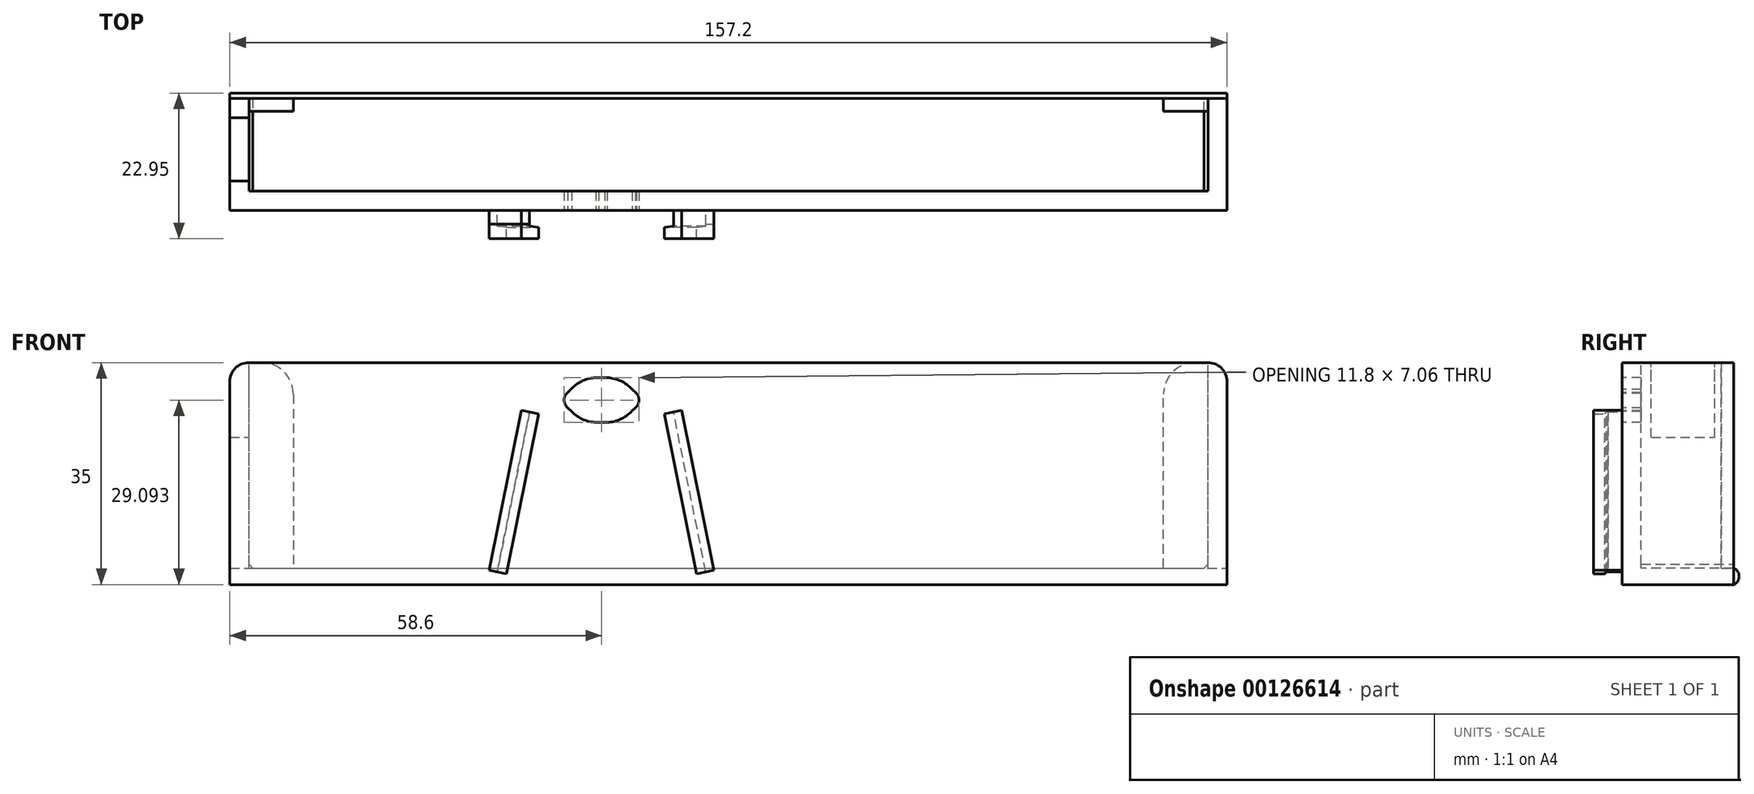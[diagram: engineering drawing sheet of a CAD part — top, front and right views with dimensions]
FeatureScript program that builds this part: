
annotation { "Feature Type Name" : "Feature", "Feature Type Description" : "" }
export const myFeature = defineFeature(function(context is Context, id is Id, definition is map)
    precondition{}
    {
        {
            var Q0;
            Q0=qCreatedBy(makeId("Front.planeOp"),FACE);
            var sketch = newSketch(context, id + "F0", { "sketchPlane" : qUnion([Q0])});
            skLineSegment(sketch, "E0", {"start": v(-29.32, 18.5) * mm, "end": v(-29.32, -6.7) * mm, "construction": true});
            skLineSegment(sketch, "E1", {"start": v(-29.32, -6.7) * mm, "end": v(-34.42, -6.7) * mm, "construction": true});
            skLineSegment(sketch, "E2", {"start": v(-29.32, 18.5) * mm, "end": v(-34.42, -6.7) * mm});
            skLineSegment(sketch, "E3", {"start": v(-34.42, -6.7) * mm, "end": v(-35.7, -6.44) * mm});
            skLineSegment(sketch, "E4", {"start": v(-35.7, -6.44) * mm, "end": v(-30.6, 18.76) * mm});
            skLineSegment(sketch, "E5", {"start": v(-29.32, 18.5) * mm, "end": v(-30.6, 18.76) * mm});
            skLineSegment(sketch, "E6", {"start": v(-30.6, 18.76) * mm, "end": v(-35.7, -6.44) * mm});
            skLineSegment(sketch, "E7", {"start": v(-29.32, 18.5) * mm, "end": v(-6.62, 18.5) * mm, "construction": true});
            skLineSegment(sketch, "E8", {"start": v(-6.62, 18.5) * mm, "end": v(-6.62, -6.7) * mm, "construction": true});
            skLineSegment(sketch, "E9", {"start": v(-6.62, -6.7) * mm, "end": v(-1.52, -6.7) * mm, "construction": true});
            skLineSegment(sketch, "E10", {"start": v(-1.52, -6.7) * mm, "end": v(-6.62, 18.5) * mm});
            skLineSegment(sketch, "E11", {"start": v(-6.62, 18.5) * mm, "end": v(-5.34, 18.76) * mm});
            skLineSegment(sketch, "E12", {"start": v(-5.34, 18.76) * mm, "end": v(-0.24, -6.44) * mm});
            skLineSegment(sketch, "E13", {"start": v(-1.52, -6.7) * mm, "end": v(-0.24, -6.44) * mm});
            skPoint(sketch, "E14.orphan", {"position": v(-0.2, -6.7) * mm});
            skLineSegment(sketch, "E15", {"start": v(-6.62, 18.5) * mm, "end": v(-6.62, 20.4) * mm, "construction": true});
            skLineSegment(sketch, "E16", {"start": v(-6.62, 20.4) * mm, "end": v(-29.32, 20.4) * mm, "construction": true});
            skLineSegment(sketch, "E17", {"start": v(-29.32, 20.4) * mm, "end": v(-29.32, 18.5) * mm, "construction": true});
            skLineSegment(sketch, "E18", {"start": v(-17.97, 20.4) * mm, "end": v(-17.97, 23.9) * mm, "construction": true});
            skLineSegment(sketch, "E19", {"start": v(-17.97, 23.9) * mm, "end": v(-17.97, 20.4) * mm, "construction": true});
            skLineSegment(sketch, "E20", {"start": v(-17.97, 20.4) * mm, "end": v(-17.97, 16.9) * mm, "construction": true});
            skPoint(sketch, "E20.endSnap0", {"position": v(-17.97, 18.5) * mm});
            skLineSegment(sketch, "E21", {"start": v(-17.97, 20.4) * mm, "end": v(-12.07, 20.4) * mm, "construction": true});
            skLineSegment(sketch, "E22", {"start": v(-17.97, 20.4) * mm, "end": v(-23.87, 20.4) * mm, "construction": true});
            skArc(sketch, "E23", {"start": v(-12.89, 19.03) * mm, "mid": v(-12.88, 19.03) * mm, "end": v(-12.87, 19.04) * mm});
            skLineSegment(sketch, "E24", {"start": v(-12.07, 20.4) * mm, "end": v(-13.64, 20.4) * mm, "construction": true});
            skLineSegment(sketch, "E25", {"start": v(-23.87, 20.4) * mm, "end": v(-22.3, 20.4) * mm, "construction": true});
            skArc(sketch, "E26", {"start": v(-23.32, 21.6) * mm, "mid": v(-23.87, 20.4) * mm, "end": v(-23.3, 19.2) * mm});
            skLineSegment(sketch, "E27", {"start": v(-23.34, 21.58) * mm, "end": v(-23.33, 21.58) * mm});
            skLineSegment(sketch, "E28", {"start": v(-23.37, 19.26) * mm, "end": v(-23.35, 19.24) * mm});
            skLineSegment(sketch, "E29", {"start": v(-17.97, 16.9) * mm, "end": v(-17.97, -14.32) * mm, "construction": true});
            skLineSegment(sketch, "E30", {"start": v(-6.62, -6.7) * mm, "end": v(-17.97, -6.7) * mm, "construction": true});
            skLineSegment(sketch, "E31", {"start": v(-17.97, -6.7) * mm, "end": v(-17.97, -8.7) * mm, "construction": true});
            skLineSegment(sketch, "E32", {"start": v(-17.97, -8.7) * mm, "end": v(80.63, -8.7) * mm});
            skLineSegment(sketch, "E33", {"start": v(80.63, -8.7) * mm, "end": v(-76.57, -8.7) * mm});
            skLineSegment(sketch, "E34.bottom", {"start": v(-76.57, -8.7) * mm, "end": v(80.63, -8.7) * mm});
            skLineSegment(sketch, "E34.top", {"start": v(-76.57, 26.3) * mm, "end": v(80.63, 26.3) * mm});
            skLineSegment(sketch, "E34.left", {"start": v(-76.57, -8.7) * mm, "end": v(-76.57, 26.3) * mm});
            skLineSegment(sketch, "E34.right", {"start": v(80.63, -8.7) * mm, "end": v(80.63, 26.3) * mm});
            skArc(sketch, "E35", {"start": v(-13.16, 22.11) * mm, "mid": v(-14.93, 23.4) * mm, "end": v(-17.06, 23.93) * mm});
            skArc(sketch, "E36", {"start": v(-18.87, 23.93) * mm, "mid": v(-20.87, 23.47) * mm, "end": v(-22.56, 22.33) * mm});
            skArc(sketch, "E37", {"start": v(-17.47, 16.87) * mm, "mid": v(-15.11, 17.33) * mm, "end": v(-13.15, 18.7) * mm});
            skLineSegment(sketch, "E38", {"start": v(-12.48, 21.46) * mm, "end": v(-13.16, 22.11) * mm});
            skLineSegment(sketch, "E39", {"start": v(-12.48, 19.35) * mm, "end": v(-13.69, 18.2) * mm});
            skLineSegment(sketch, "E40", {"start": v(-23.46, 19.35) * mm, "end": v(-22.4, 18.32) * mm});
            skLineSegment(sketch, "E41", {"start": v(-23.46, 21.46) * mm, "end": v(-22.56, 22.33) * mm});
            skLineSegment(sketch, "E42", {"start": v(-17.06, 23.93) * mm, "end": v(-18.87, 23.93) * mm});
            skLineSegment(sketch, "E43", {"start": v(-17.47, 16.87) * mm, "end": v(-18.77, 16.87) * mm});
            skArc(sketch, "E44.trimOffspring", {"start": v(-12.64, 19.2) * mm, "mid": v(-12.07, 20.3) * mm, "end": v(-12.48, 21.46) * mm});
            skArc(sketch, "E45.trimOffspring", {"start": v(-22.7, 18.62) * mm, "mid": v(-20.75, 17.3) * mm, "end": v(-18.43, 16.87) * mm});
            skSolve(sketch);
        }
        {
            var Q0;
            Q0=makeQuery(id+"F0.imprint","IMPRINT",FACE,{"disambiguationData":[TD([[makeQuery(id+"F0.imprint","IMPRINT",EDGE,{"derivedFrom":sQuery(id+"F0.wireOp",EDGE,"E10")}),-1.0]])]});
            var Q1;
            Q1=makeQuery(id+"F0.imprint","IMPRINT",FACE,{"disambiguationData":[TD([[makeQuery(id+"F0.imprint","IMPRINT",EDGE,{"derivedFrom":sQuery(id+"F0.wireOp",EDGE,"E2")}),-1.0]])]});
            extrude(context, id + "F1", {"entities" : qUnion([Q0, Q1]), "depth" : 2.2 * mm});
        }
        {
            var Q0;
            Q0=makeQuery(id+"F1.opExtrude","SWEPT_FACE",FACE,{"disambiguationData":[OSD([sQuery(id+"F0.wireOp",EDGE,"E5")])]});
            var sketch = newSketch(context, id + "F2", { "sketchPlane" : qUnion([Q0])});
            skLineSegment(sketch, "E46", {"start": v(-33.7, 0) * mm, "end": v(-33.7, -4.5) * mm});
            skLineSegment(sketch, "E47", {"start": v(-33.7, -4.5) * mm, "end": v(-30.9, -4.5) * mm});
            skLineSegment(sketch, "E48", {"start": v(-30.9, -4.5) * mm, "end": v(-30.9, -2.7) * mm});
            skLineSegment(sketch, "E49", {"start": v(-32.4, 0) * mm, "end": v(-32.4, -2.5) * mm, "construction": true});
            skLineSegment(sketch, "E50", {"start": v(-30.9, -2.7) * mm, "end": v(-32.4, -2.5) * mm});
            skLineSegment(sketch, "E51", {"start": v(-32.4, -2.5) * mm, "end": v(-32.4, 0) * mm});
            skLineSegment(sketch, "E52", {"start": v(-32.4, -2.2) * mm, "end": v(-33.7, -2.2) * mm});
            skSolve(sketch);
        }
        {
            var Q0;
            Q0 = qSketchRegion(id + "F2", true);
            var Q1;
            {var subQ0=sQuery(id+"F2.wireOp",EDGE,"E47");Q1=makeQuery(id+"F2.imprint","IMPRINT",FACE,{"disambiguationData":[TD([[makeQuery(id+"F2.imprint","IMPRINT",EDGE,{"derivedFrom":subQ0}),1.0]])]});}
            extrude(context, id + "F3", {"entities" : qUnion([Q0, Q1]), "oppositeDirection" : true, "depth" : 25.7 * mm});
        }
        {
            var Q0;
            Q0=makeQuery(id+"F1.opExtrude","SWEPT_FACE",FACE,{"disambiguationData":[OSD([sQuery(id+"F0.wireOp",EDGE,"E11")])]});
            var sketch = newSketch(context, id + "F4", { "sketchPlane" : qUnion([Q0])});
            skLineSegment(sketch, "E53", {"start": v(-1.52, 0) * mm, "end": v(-1.52, -4.5) * mm});
            skLineSegment(sketch, "E54", {"start": v(-1.52, -4.5) * mm, "end": v(-4.32, -4.5) * mm});
            skLineSegment(sketch, "E55", {"start": v(-4.32, -4.5) * mm, "end": v(-4.32, -2.7) * mm});
            skLineSegment(sketch, "E56", {"start": v(-2.82, 0) * mm, "end": v(-2.82, -2.5) * mm, "construction": true});
            skLineSegment(sketch, "E57", {"start": v(-4.32, -2.7) * mm, "end": v(-2.82, -2.5) * mm});
            skLineSegment(sketch, "E58", {"start": v(-2.82, -2.5) * mm, "end": v(-2.82, -2.2) * mm});
            skSolve(sketch);
        }
        {
            var Q0;
            Q0 = qSketchRegion(id + "F4", true);
            var Q1;
            {var subQ1=sQuery(id+"F4.wireOp",EDGE,"E54");Q1=makeQuery(id+"F4.imprint","IMPRINT",FACE,{"disambiguationData":[TD([[makeQuery(id+"F4.imprint","IMPRINT",EDGE,{"derivedFrom":subQ1}),-1.0]])]});}
            extrude(context, id + "F5", {"entities" : qUnion([Q0, Q1]), "operationType" : NewBodyOperationType.ADD, "oppositeDirection" : true, "depth" : 25.7 * mm});
        }
        {
            var Q0;
            Q0 = qSketchRegion(id + "F0", true);
            var Q1;
            Q1=makeQuery(id+"F0.imprint","IMPRINT",FACE,{"disambiguationData":[TD([[makeQuery(id+"F0.imprint","IMPRINT",EDGE,{"derivedFrom":sQuery(id+"F0.wireOp",EDGE,"E2")}),-1.0]])]});
            var Q2;
            Q2=makeQuery(id+"F0.imprint","IMPRINT",FACE,{"disambiguationData":[TD([[makeQuery(id+"F0.imprint","IMPRINT",EDGE,{"derivedFrom":sQuery(id+"F0.wireOp",EDGE,"E10")}),-1.0]])]});
            extrude(context, id + "F6", {"entities" : qUnion([Q0, Q1, Q2]), "oppositeDirection" : true, "depth" : 3 * mm});
        }
        {
            var Q0;
            Q0=makeQuery(id+"F6.opExtrude","CAP_FACE",FACE,{"disambiguationData":[OSD([sQuery(id+"F0.wireOp",EDGE,"MNrqED6R-0Bs3-LNVi-oEKI-MaJAXrPDSpCK"),sQuery(id+"F0.wireOp",EDGE,"FX8ncu83-0Qzv-e0OL-q1TA-2oPik7mIZz2Z"),sQuery(id+"F0.wireOp",EDGE,"E23"),sQuery(id+"F0.wireOp",EDGE,"E26"),sQuery(id+"F0.wireOp",EDGE,"E27"),sQuery(id+"F0.wireOp",EDGE,"E28"),sQuery(id+"F0.wireOp",EDGE,"ljumUwIM-9yZB-9kN5-kGQy-0t9YJfCgj0Kk"),sQuery(id+"F0.wireOp",EDGE,"Kp9V1Czn-WVNw-DR18-KSKj-JMUbyk1VQTje"),sQuery(id+"F0.wireOp",EDGE,"E34.bottom"),sQuery(id+"F0.wireOp",EDGE,"E34.top"),sQuery(id+"F0.wireOp",EDGE,"E34.left"),sQuery(id+"F0.wireOp",EDGE,"E34.right")])],"isStart":false});
            var sketch = newSketch(context, id + "F7", { "sketchPlane" : qUnion([Q0])});
            skLineSegment(sketch, "E59.1", {"start": v(73.57, -6.1) * mm, "end": v(73.57, 40.7) * mm});
            skLineSegment(sketch, "E59.2", {"start": v(73.57, -6.1) * mm, "end": v(-77.63, -6.1) * mm});
            skLineSegment(sketch, "E59.3", {"start": v(-77.63, -6.1) * mm, "end": v(-77.63, 40.7) * mm});
            skLineSegment(sketch, "E60", {"start": v(73.57, 26.3) * mm, "end": v(73.57, 40.7) * mm});
            skLineSegment(sketch, "E61", {"start": v(-77.63, -6.1) * mm, "end": v(-77.63, 26.3) * mm});
            skSolve(sketch);
        }
        {
            var Q0;
            Q0 = qSketchRegion(id + "F7", true);
            var Q1;
            Q1=makeQuery(id+"F7.imprint","IMPRINT",FACE,{"disambiguationData":[TD([[makeQuery(id+"F7.imprint","IMPRINT",EDGE,{"derivedFrom":sQuery(id+"F7.wireOp",EDGE,"E59.1")}),-1.0]])]});
            extrude(context, id + "F8", {"entities" : qUnion([Q0, Q1]), "operationType" : NewBodyOperationType.ADD, "depth" : (12 + 2.6) * mm});
        }
        {
            var Q0;
            Q0=makeQuery(id+"F8.opExtrude","CAP_FACE",FACE,{"disambiguationData":[OSD([sQuery(id+"F0.wireOp",EDGE,"E34.bottom"),sQuery(id+"F0.wireOp",EDGE,"E34.top"),sQuery(id+"F0.wireOp",EDGE,"E34.left"),sQuery(id+"F0.wireOp",EDGE,"E34.right"),sQuery(id+"F7.wireOp",EDGE,"E59.1"),sQuery(id+"F7.wireOp",EDGE,"E59.2"),sQuery(id+"F7.wireOp",EDGE,"E59.3"),sQuery(id+"F7.wireOp",EDGE,"EL1yQ1mo-xAsi-Qadm-DahA-Dr1vwk5fQx9r"),sQuery(id+"F7.wireOp",EDGE,"E60")])],"isStart":false});
            var sketch = newSketch(context, id + "F9", { "sketchPlane" : qUnion([Q0])});
            skLineSegment(sketch, "E62", {"start": v(76.57, 26.3) * mm, "end": v(66.57, 26.3) * mm});
            skLineSegment(sketch, "E63", {"start": v(66.57, 26.3) * mm, "end": v(66.57, -6.1) * mm});
            skLineSegment(sketch, "E64", {"start": v(-77.63, 26.3) * mm, "end": v(-70.63, 26.3) * mm});
            skLineSegment(sketch, "E65", {"start": v(-70.63, -6.1) * mm, "end": v(-70.63, 26.3) * mm});
            skLineSegment(sketch, "E66", {"start": v(73.57, 26.3) * mm, "end": v(73.57, -6.1) * mm});
            skSolve(sketch);
        }
        {
            var Q0;
            Q0 = qSketchRegion(id + "F9", true);
            var Q1;
            {var subQ2=sQuery(id+"F9.wireOp",EDGE,"5CY6TRSu-ZqDC-SEN2-w5CQ-rCevLjkbbSBQ");Q1=makeQuery(id+"F9.imprint","IMPRINT",FACE,{"disambiguationData":[TD([[makeQuery(id+"F9.imprint","IMPRINT",EDGE,{"derivedFrom":subQ2}),-1.0]])]});}
            var Q2;
            Q2=makeQuery(id+"F9.imprint","IMPRINT",FACE,{"disambiguationData":[TD([[makeQuery(id+"F9.imprint","IMPRINT",EDGE,{"derivedFrom":sQuery(id+"F9.wireOp",EDGE,"E62")}),1.0]])]});
            var Q3;
            Q3=makeQuery(id+"F9.imprint","IMPRINT",FACE,{"disambiguationData":[TD([[makeQuery(id+"F9.imprint","IMPRINT",EDGE,{"derivedFrom":sQuery(id+"F9.wireOp",EDGE,"E64")}),-1.0]])]});
            extrude(context, id + "F10", {"entities" : qUnion([Q0, Q1, Q2, Q3]), "oppositeDirection" : true, "depth" : 2 * mm});
        }
        {
            var Q0;
            {var subQ0=sQuery(id+"F0.wireOp",EDGE,"E34.right");Q0=makeQuery(id+"F8.boolean.opBoolean","MERGE",FACE,{"derivedFrom":[makeQuery(id+"F6.opExtrude","SWEPT_FACE",FACE,{"disambiguationData":[OSD([subQ0])]}),makeQuery(id+"F8.opExtrude","SWEPT_FACE",FACE,{"disambiguationData":[OSD([subQ0])]})]});}
            var sketch = newSketch(context, id + "F11", { "sketchPlane" : qUnion([Q0])});
            skPoint(sketch, "E67.0", {"position": v(17.6, -8.7) * mm});
            skLineSegment(sketch, "E68", {"start": v(17.6, -4.66) * mm, "end": v(17.6, -8.7) * mm});
            skPoint(sketch, "E69.0", {"position": v(17.6, -6.1) * mm});
            skArc(sketch, "E70", {"start": v(17.6, -8.7) * mm, "mid": v(18.45, -7.4) * mm, "end": v(17.6, -6.1) * mm});
            skSolve(sketch);
        }
        {
            var Q0;
            Q0 = qSketchRegion(id + "F11", true);
            extrude(context, id + "F12", {"entities" : qUnion([Q0]), "oppositeDirection" : true, "depth" : 157.2 * mm});
        }
        {
            var Q0;
            Q0=makeQuery(id+"F10.opExtrude","SWEPT_EDGE",EDGE,{"disambiguationData":[OSD([sQuery(id+"F9.wireOp",EDGE,"E62"),sQuery(id+"F9.wireOp",EDGE,"E63")])]});
            var Q1;
            Q1=makeQuery(id+"F10.opExtrude","SWEPT_EDGE",EDGE,{"disambiguationData":[OSD([sQuery(id+"F9.wireOp",EDGE,"E64"),sQuery(id+"F9.wireOp",EDGE,"E65")])]});
            fillet(context, id + "F13", {"entities" : qUnion([Q0, Q1]), "radius" : 5 * mm, "tangentPropagation" : true, "allowEdgeOverflow" : false});
        }
        {
            var Q0;
            Q0=makeQuery(id+"F8.opExtrude","CAP_EDGE",EDGE,{"disambiguationData":[OSD([sQuery(id+"F7.wireOp",EDGE,"E59.2")])],"isStart":true});
            var Q1;
            Q1=makeQuery(id+"F8.opExtrude","SWEPT_EDGE",EDGE,{"disambiguationData":[OSD([sQuery(id+"F7.wireOp",EDGE,"E59.1"),sQuery(id+"F7.wireOp",EDGE,"E59.2")])]});
            var Q2;
            Q2=makeQuery(id+"F8.opExtrude","SWEPT_EDGE",EDGE,{"disambiguationData":[OSD([sQuery(id+"F7.wireOp",EDGE,"E59.2"),sQuery(id+"F7.wireOp",EDGE,"E59.3")])]});
            var Q3;
            Q3=makeQuery(id+"F8.opExtrude","CAP_EDGE",EDGE,{"disambiguationData":[OSD([sQuery(id+"F7.wireOp",EDGE,"E59.3"),sQuery(id+"F7.wireOp",EDGE,"EL1yQ1mo-xAsi-Qadm-DahA-Dr1vwk5fQx9r")])],"isStart":true});
            var Q4;
            Q4=makeQuery(id+"F8.opExtrude","CAP_EDGE",EDGE,{"disambiguationData":[OSD([sQuery(id+"F7.wireOp",EDGE,"E59.1"),sQuery(id+"F7.wireOp",EDGE,"E60")])],"isStart":true});
            var Q5;
            Q5=makeQuery(id+"F10.opExtrude","CAP_EDGE",EDGE,{"disambiguationData":[OSD([sQuery(id+"F9.wireOp",EDGE,"Ge6mcemf-SlfB-CZ4T-F4Ns-TyBtLsnh8UQz.top")])],"isStart":false});
            chamfer(context, id + "F14", {"entities" : qUnion([Q0, Q1, Q2, Q3, Q4, Q5]), "width" : 0.6 * mm, "tangentPropagation" : true});
        }
        {
            var Q0;
            Q0=makeQuery(id+"F8.opExtrude","SWEPT_FACE",FACE,{"disambiguationData":[OSD([sQuery(id+"F7.wireOp",EDGE,"E59.1")])]});
            var sketch = newSketch(context, id + "F15", { "sketchPlane" : qUnion([Q0])});
            skLineSegment(sketch, "E71", {"start": v(3.6, -2.38) * mm, "end": v(4.6, -2.38) * mm, "construction": true});
            skLineSegment(sketch, "E72.0", {"start": v(15.6, -6.1) * mm, "end": v(15.6, 26.3) * mm, "construction": true});
            skLineSegment(sketch, "E73", {"start": v(15.6, -5.5) * mm, "end": v(14.6, -5.5) * mm, "construction": true});
            skLineSegment(sketch, "E74", {"start": v(4.6, 14.5) * mm, "end": v(14.6, 14.5) * mm});
            skLineSegment(sketch, "E75", {"start": v(4.6, 14.5) * mm, "end": v(4.6, 26.3) * mm});
            skLineSegment(sketch, "E76", {"start": v(14.6, 14.5) * mm, "end": v(14.6, 26.3) * mm});
            skPoint(sketch, "E77.start.orphan", {"position": v(4.6, -5.5) * mm});
            skSolve(sketch);
        }
        {
            var Q0;
            Q0=makeQuery(id+"F15.imprint","IMPRINT",FACE,{"disambiguationData":[TD([[makeQuery(id+"F15.imprint","IMPRINT",EDGE,{"derivedFrom":sQuery(id+"F15.wireOp",EDGE,"E74")}),1.0]])]});
            extrude(context, id + "F16", {"entities" : qUnion([Q0]), "operationType" : NewBodyOperationType.REMOVE, "oppositeDirection" : true, "depth" : 25 * mm});
        }
        {
            var Q0;
            {var subQ0=sQuery(id+"F0.wireOp",EDGE,"E34.right");var subQ1=sQuery(id+"F0.wireOp",EDGE,"E34.top");Q0=makeQuery(id+"F8.boolean.opBoolean","MERGE",EDGE,{"derivedFrom":[makeQuery(id+"F6.opExtrude","SWEPT_EDGE",EDGE,{"disambiguationData":[OSD([subQ1,subQ0])]}),makeQuery(id+"F8.opExtrude","SWEPT_EDGE",EDGE,{"disambiguationData":[OSD([subQ1,subQ0])]})]});}
            var Q1;
            {var subQ0=sQuery(id+"F0.wireOp",EDGE,"E34.left");var subQ4=sQuery(id+"F0.wireOp",EDGE,"E34.top");Q1=makeQuery(id+"F16.boolean.opBoolean","SPLIT",EDGE,{"disambiguationData":[TD([makeQuery(id+"F16.opExtrude","SWEPT_FACE",FACE,{"disambiguationData":[OSD([sQuery(id+"F15.wireOp",EDGE,"E76")])]})])],"derivedFrom":makeQuery(id+"F8.boolean.opBoolean","MERGE",EDGE,{"derivedFrom":[makeQuery(id+"F6.opExtrude","SWEPT_EDGE",EDGE,{"disambiguationData":[OSD([subQ4,subQ0])]}),makeQuery(id+"F8.opExtrude","SWEPT_EDGE",EDGE,{"disambiguationData":[OSD([subQ4,subQ0])]})]})});}
            var Q2;
            {var subQ0=sQuery(id+"F0.wireOp",EDGE,"E34.left");var subQ1=sQuery(id+"F0.wireOp",EDGE,"E34.top");Q2=makeQuery(id+"F16.boolean.opBoolean","SPLIT",EDGE,{"disambiguationData":[TD([makeQuery(id+"F16.opExtrude","SWEPT_FACE",FACE,{"disambiguationData":[OSD([sQuery(id+"F15.wireOp",EDGE,"E75")])]})])],"derivedFrom":makeQuery(id+"F8.boolean.opBoolean","MERGE",EDGE,{"derivedFrom":[makeQuery(id+"F6.opExtrude","SWEPT_EDGE",EDGE,{"disambiguationData":[OSD([subQ1,subQ0])]}),makeQuery(id+"F8.opExtrude","SWEPT_EDGE",EDGE,{"disambiguationData":[OSD([subQ1,subQ0])]})]})});}
            fillet(context, id + "F17", {"entities" : qUnion([Q0, Q1, Q2]), "radius" : 3 * mm, "tangentPropagation" : true, "allowEdgeOverflow" : false});
        }
    });
